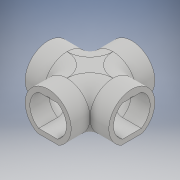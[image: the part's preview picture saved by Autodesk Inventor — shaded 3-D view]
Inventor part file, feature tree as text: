
AUTODESK INVENTOR PART (.ipt)
format: ipt  version: 2017 (Build 210142000, 142)  size: 486,400 bytes
history: native  units: in
note: dims shown in document units (in); Inventor stores cm internally (conversion verified against a paired STEP export)
features: sketch x6, extrude x5, mirror x4, other x3, sweep x2, plane x1, fillet x1
ambient origin geometry x8: Origin, YZ Plane, XZ Plane, XY Plane, X Axis, Y Axis, Z Axis, Center Point
bodies: Body1 (feature_tree), Body2 (feature_tree), Body3 (feature_tree)
feature tree (22):
  sketch  "Sketch1"  dims[d0=6.6667in d2=9.7746in d5=-4.8873in d49=0.0625in]
  extrude  "corridor eighth"  Depth=0.0625in
  plane  "Work Plane1"
  extrude  "light quarter eighth"  Depth=4.0in TaperAngle=0.0deg
  sketch  "Sketch17"  dims[d153=0.25in d154=0.0417in]
  sketch  "Sketch7"  dims[d62=45.0deg d71=4.0in d72=0.0in]
  sweep  "sweep corridor quarter"
  sweep  "light sweep quarter"
  mirror  "mirror plane YZ"
  mirror  "mirror plane XY"
  mirror  "mirror corridor half"
  mirror  "mirror corridor full"
  extrude  "top hole fill"  Depth=4.0in TaperAngle=0.0deg
  extrude  "top fill in for light"  TaperAngle=0.0deg  [1 undecoded]
  fillet  "Fillet1"  [1 undecoded]
  extrude  "bottom hole fill in"  Depth=0.0625in TaperAngle=0.0deg
  other  "corridor"
  other  "light eighth"
  other  "light forth"
  sketch  "Sketch19"  dims[d155=0.0625in d156=0.0892in]
  sketch  "Sketch20"  dims[d157=0.125in d158=4.0in d159=0.0in]
  sketch  "Sketch21"  dims[d160=4.0in d161=0.0in d162=0.0in d163=0.0in d164=0.0in d165=1.429in d166=0.0in d167=1.554in d168=10.3167in d169=10.3167in d170=10.3167in d171=10.3167in d172=5.1583in d173=5.1583in d174=5.1583in d175=5.1583in d176=0.125in d177=0.0in d178=0.0625in d179=1.0in d180=0.0in]
note: 2 required parameter values undecoded (feature->parameter linkage not recoverable at this tier; creation-order binding heuristic only, values carry confidence <= 0.55)
